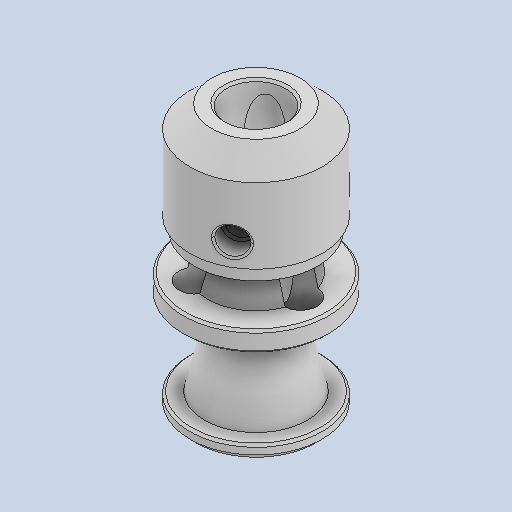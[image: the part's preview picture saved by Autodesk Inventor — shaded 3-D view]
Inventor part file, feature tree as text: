
AUTODESK INVENTOR PART (.ipt)
format: ipt  version: 2024 (Build 280153000, 153)  size: 390,656 bytes
history: native  units: in
note: dims shown in document units (in); Inventor stores cm internally (conversion verified against a paired STEP export)
features: chamfer x1
ambient origin geometry x8: Origin, YZ Plane, XZ Plane, XY Plane, X Axis, Y Axis, Z Axis, Center Point
bodies: Solid1 (feature_tree)
feature tree (1):
  chamfer  "Chamfer6"  [1 undecoded]
note: 1 required parameter value undecoded (feature->parameter linkage not recoverable at this tier; creation-order binding heuristic only, values carry confidence <= 0.55)
